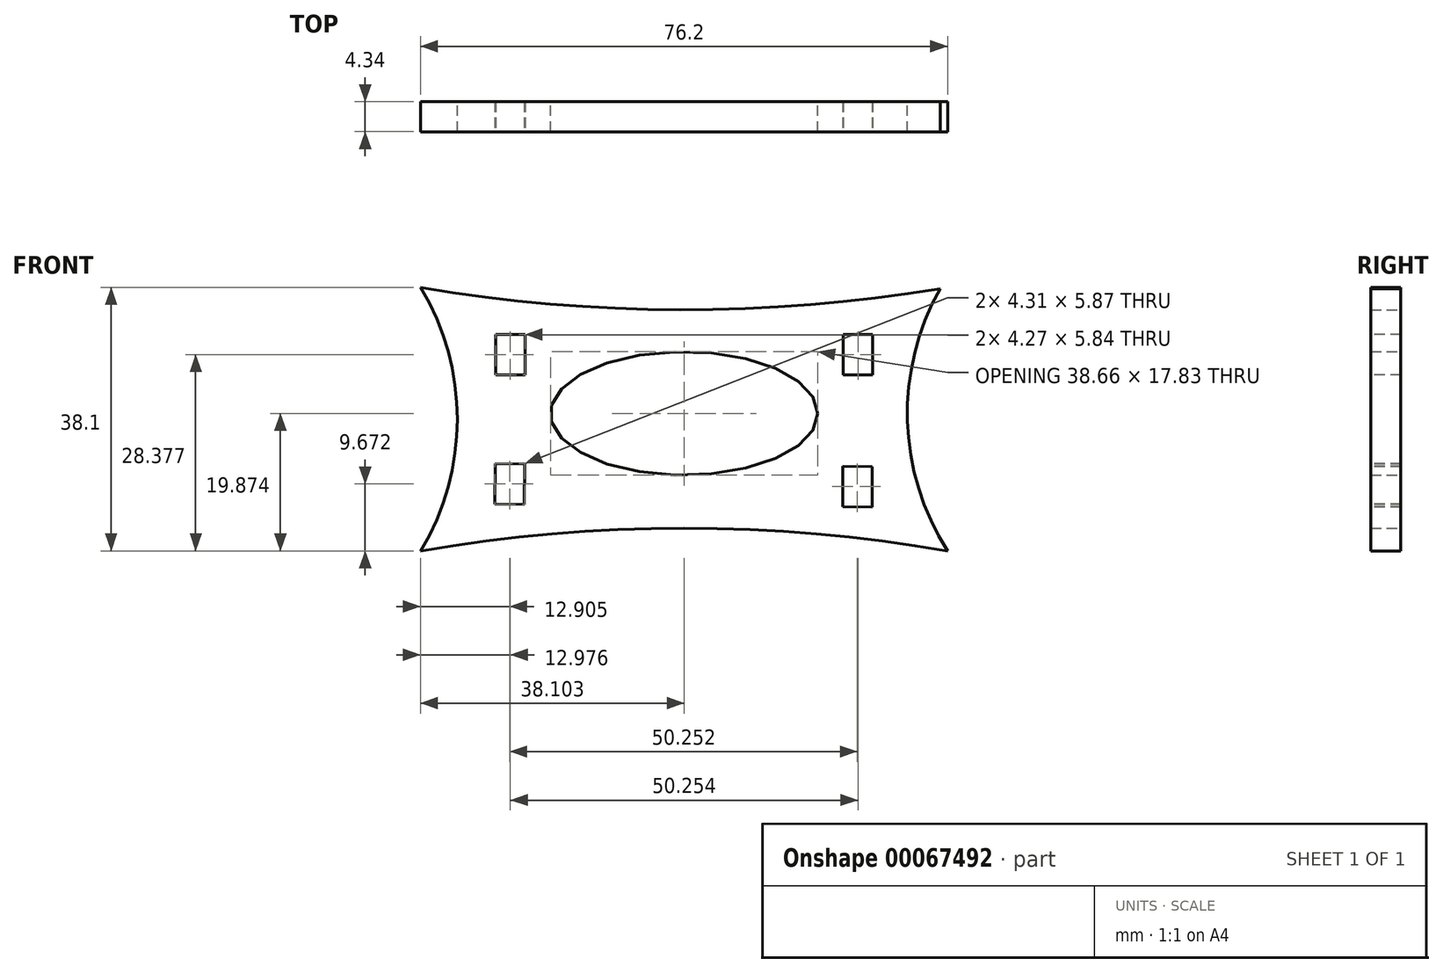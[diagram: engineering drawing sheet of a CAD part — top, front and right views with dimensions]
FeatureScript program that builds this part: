
annotation { "Feature Type Name" : "Feature", "Feature Type Description" : "" }
export const myFeature = defineFeature(function(context is Context, id is Id, definition is map)
    precondition{}
    {
        {
            var Q0;
            Q0=qCreatedBy(makeId("Front.planeOp"),FACE);
            var sketch = newSketch(context, id + "F0", { "sketchPlane" : qUnion([Q0])});
            skArc(sketch, "E0", {"start": v(-28.52, -28.29) * mm, "mid": v(-23.2, -9.24) * mm, "end": v(-28.52, 9.81) * mm});
            skArc(sketch, "E1.MirrorCS", {"start": v(47.68, -28.29) * mm, "mid": v(41.85, -8.42) * mm, "end": v(47.68, 11.45) * mm});
            skPoint(sketch, "E2.end.orphan", {"position": v(9.58, -26.65) * mm});
            skPoint(sketch, "E2.start.orphan", {"position": v(9.58, 9.81) * mm});
            skArc(sketch, "E3", {"start": v(-28.52, 9.81) * mm, "mid": v(9.58, 6.57) * mm, "end": v(47.68, 9.81) * mm});
            skArc(sketch, "E4.MirrorCS", {"start": v(-28.52, -28.29) * mm, "mid": v(9.58, -25.01) * mm, "end": v(47.68, -28.29) * mm});
            skLineSegment(sketch, "E5.trimOffspring", {"start": v(46.69, -26.65) * mm, "end": v(47.68, -26.65) * mm});
            skPoint(sketch, "E6.end.orphan", {"position": v(41.85, -8.42) * mm});
            skPoint(sketch, "E6.start.orphan", {"position": v(-23.2, -9.24) * mm});
            skPoint(sketch, "E7.centerSnap0", {"position": v(9.58, 6.57) * mm});
            skPoint(sketch, "E7.center.orphan", {"position": v(9.58, -8.42) * mm});
            skEllipse(sketch, "E8", {"center": v(9.58, -8.42) * mm, "majorRadius": 19.33 * mm, "minorRadius": 8.92 * mm, "majorAxis": v(1, 0)});
            skLineSegment(sketch, "E9", {"start": v(-28.52, 9.81) * mm, "end": v(-28.52, -28.29) * mm, "construction": true});
            skLineSegment(sketch, "E10", {"start": v(-28.52, -28.29) * mm, "end": v(47.68, -28.29) * mm, "construction": true});
            skPoint(sketch, "E11.top.start.orphan", {"position": v(-28.52, -26.65) * mm});
            skLineSegment(sketch, "E12", {"start": v(9.58, 6.57) * mm, "end": v(9.58, -25.01) * mm, "construction": true});
            skSolve(sketch);
        }
        {
            var Q0;
            Q0 = qSketchRegion(id + "F0", true);
            extrude(context, id + "F1", {"entities" : qUnion([Q0]), "depth" : 4.34 * mm});
        }
        {
            var Q0;
            Q0=makeQuery(id+"F1.opExtrude","CAP_FACE",FACE,{"disambiguationData":[OSD([sQuery(id+"F0.wireOp",EDGE,"E0"),sQuery(id+"F0.wireOp",EDGE,"E1.MirrorCS"),sQuery(id+"F0.wireOp",EDGE,"E3"),sQuery(id+"F0.wireOp",EDGE,"E4.MirrorCS"),sQuery(id+"F0.wireOp",EDGE,"E8")])],"isStart":false});
            var sketch = newSketch(context, id + "F2", { "sketchPlane" : qUnion([Q0])});
            skPoint(sketch, "E13.orphan", {"position": v(-23.2, -9.24) * mm});
            skPoint(sketch, "E14.end.orphan", {"position": v(41.87, -9.48) * mm});
            skPoint(sketch, "E15.end.orphan", {"position": v(9.58, -17.33) * mm});
            skPoint(sketch, "E15.start.orphan", {"position": v(9.58, 0.5) * mm});
            skLineSegment(sketch, "E16", {"start": v(-28.52, 9.81) * mm, "end": v(-28.52, -28.29) * mm, "construction": true});
            skLineSegment(sketch, "E17", {"start": v(-28.52, -28.29) * mm, "end": v(47.68, -28.29) * mm, "construction": true});
            skPoint(sketch, "E18.middle", {"position": v(-15.54, 0.09) * mm});
            skPoint(sketch, "E19.MirrorC.center.orphan", {"position": v(34.75, 2.62) * mm});
            skPoint(sketch, "E20.orphan", {"position": v(9.03, 6.57) * mm});
            skPoint(sketch, "E21.orphan", {"position": v(-28.52, -9.24) * mm});
            skPoint(sketch, "E22.endSnap0", {"position": v(9.58, -25.01) * mm});
            skPoint(sketch, "E23.start.orphan", {"position": v(34.75, 5.16) * mm});
            skPoint(sketch, "E24.MirrorCS.end.orphan", {"position": v(46.57, 1.65) * mm});
            skPoint(sketch, "E24.MirrorCS.start.orphan", {"position": v(33.63, 1.65) * mm});
            skPoint(sketch, "E25.MirrorCS.end.orphan", {"position": v(-35.85, -25.01) * mm});
            skPoint(sketch, "E25.MirrorCS.start.orphan", {"position": v(-35.85, 6.57) * mm});
            skPoint(sketch, "E22.end.orphan", {"position": v(9.03, -25.01) * mm});
            skLineSegment(sketch, "E26", {"start": v(9.58, 0.5) * mm, "end": v(9.58, -17.33) * mm, "construction": true});
            skLineSegment(sketch, "E27", {"start": v(-23.2, -9.24) * mm, "end": v(41.87, -9.48) * mm, "construction": true});
            skPoint(sketch, "E28.MirrorP", {"position": v(34.66, -21.53) * mm});
            skPoint(sketch, "E29.endSnap0", {"position": v(-15.54, 3) * mm});
            skLineSegment(sketch, "E30", {"start": v(9.03, 6.57) * mm, "end": v(-26.8, 6.65) * mm, "construction": true});
            skPoint(sketch, "E31.trimOffspring.end.orphan", {"position": v(-15.54, 7.97) * mm});
            skLineSegment(sketch, "E32", {"start": v(-15.54, 0.09) * mm, "end": v(-15.54, 6.63) * mm, "construction": true});
            skLineSegment(sketch, "E33.bottom", {"start": v(-17.68, 3) * mm, "end": v(-13.41, 3) * mm});
            skLineSegment(sketch, "E33.top", {"start": v(-17.68, -2.83) * mm, "end": v(-13.41, -2.83) * mm});
            skLineSegment(sketch, "E33.left", {"start": v(-17.68, 3) * mm, "end": v(-17.68, -2.83) * mm});
            skLineSegment(sketch, "E33.right", {"start": v(-13.41, 3) * mm, "end": v(-13.41, -2.83) * mm});
            skPoint(sketch, "E34.positionSnap0", {"position": v(-13.41, 0.09) * mm});
            skPoint(sketch, "E35.MirrorCS.end.orphan", {"position": v(36.8, -25.28) * mm});
            skPoint(sketch, "E35.MirrorCS.start.orphan", {"position": v(32.46, -25.24) * mm});
            skPoint(sketch, "E36.MirrorCS.start.orphan", {"position": v(32.5, -18.9) * mm});
            skPoint(sketch, "E37.MirrorCS.start.orphan", {"position": v(36.85, -18.93) * mm});
            skPoint(sketch, "E38.MirrorCS.end.orphan", {"position": v(36.92, 0) * mm});
            skPoint(sketch, "E38.MirrorCS.start.orphan", {"position": v(32.58, 0) * mm});
            skPoint(sketch, "E39.MirrorCS.end.orphan", {"position": v(36.92, 6.35) * mm});
            skPoint(sketch, "E40.MirrorCS.start.orphan", {"position": v(32.58, 6.35) * mm});
            skLineSegment(sketch, "E41", {"start": v(-15.54, 0.09) * mm, "end": v(-28.52, 0.09) * mm, "construction": true});
            skLineSegment(sketch, "E42.MirrorCS", {"start": v(36.84, -2.83) * mm, "end": v(32.58, -2.83) * mm});
            skLineSegment(sketch, "E43.MirrorCS", {"start": v(32.58, 3) * mm, "end": v(32.58, -2.83) * mm});
            skLineSegment(sketch, "E44.MirrorCS", {"start": v(36.84, 3) * mm, "end": v(32.58, 3) * mm});
            skLineSegment(sketch, "E45.MirrorCS", {"start": v(36.84, 3) * mm, "end": v(36.84, -2.83) * mm});
            skLineSegment(sketch, "E46.MirrorCS", {"start": v(-17.73, -15.68) * mm, "end": v(-13.46, -15.71) * mm});
            skLineSegment(sketch, "E47.MirrorCS", {"start": v(-13.5, -21.55) * mm, "end": v(-13.46, -15.71) * mm});
            skLineSegment(sketch, "E48.MirrorCS", {"start": v(-17.77, -21.52) * mm, "end": v(-13.5, -21.55) * mm});
            skLineSegment(sketch, "E49.MirrorCS", {"start": v(-17.77, -21.52) * mm, "end": v(-17.73, -15.68) * mm});
            skLineSegment(sketch, "E50.MirrorCS", {"start": v(36.8, -16.1) * mm, "end": v(32.53, -16.06) * mm});
            skLineSegment(sketch, "E51.MirrorCS", {"start": v(32.48, -21.9) * mm, "end": v(32.53, -16.06) * mm});
            skLineSegment(sketch, "E52.MirrorCS", {"start": v(36.75, -21.93) * mm, "end": v(32.48, -21.9) * mm});
            skLineSegment(sketch, "E53.MirrorCS", {"start": v(36.75, -21.93) * mm, "end": v(36.8, -16.1) * mm});
            skSolve(sketch);
        }
        {
            var Q0;
            Q0 = qSketchRegion(id + "F2", true);
            extrude(context, id + "F3", {"entities" : qUnion([Q0]), "operationType" : NewBodyOperationType.REMOVE, "endBound" : BoundingType.THROUGH_ALL, "oppositeDirection" : true, "depth" : 25.4 * mm});
        }
    });
